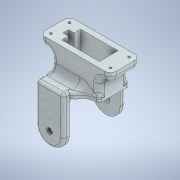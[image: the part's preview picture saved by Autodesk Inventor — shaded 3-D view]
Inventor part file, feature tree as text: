
AUTODESK INVENTOR PART (.ipt)
format: ipt  version: 2021 (Build 250183000, 183)  size: 626,176 bytes
history: native  units: mm
features: sketch x9, extrude x8, fillet x7, projected_geometry x2, plane x1
ambient origin geometry x8: Origin, YZ Plane, XZ Plane, XY Plane, X Axis, Y Axis, Z Axis, Center Point
bodies: Solid1 (feature_tree)
feature tree (27):
  extrude  "Extrusion1"  Depth=30.0mm
  extrude  "Extrusion2"  Depth=2.5mm TaperAngle=0.0deg
  plane  "Work Plane1"
  extrude  "Extrusion3"  Depth=3.5mm TaperAngle=0.0deg
  sketch  "Sketch4"  dims[d8=54.7mm d9=7.8mm d10=6.0mm d11=0.0mm]
  extrude  "Extrusion4"  Depth=7.8mm
  fillet  "Fillet1"  Radius=6.0mm
  extrude  "Extrusion5"  Depth=6.0mm
  extrude  "Extrusion6"  Depth=20.0mm
  extrude  "Extrusion7"  Depth=10.0mm
  fillet  "Fillet2"  Radius=6.0mm
  fillet  "Fillet3"  Radius=27.0mm
  fillet  "Fillet4"  Radius=27.0mm
  fillet  "Fillet5"  Radius=6.0mm
  fillet  "Fillet7"  Radius=7.0mm
  extrude  "Extrusion8"  Depth=10.0mm
  fillet  "Fillet8"  Radius=12.0mm
  sketch  "Sketch1"  dims[d0=20.6mm d1=30.0mm]
  sketch  "Sketch2"  dims[d2=35.0mm d3=2.5mm d4=0.0mm]
  projected_geometry  "Projected Loop1"
  sketch  "Sketch3"  dims[d5=6.0mm d6=3.5mm d7=0.0mm]
  projected_geometry  "Projected Loop2"
  sketch  "Sketch5"  dims[d12=6.0mm d13=0.0mm d14=6.0mm]
  sketch  "Sketch6"  dims[d15=40.0mm d16=20.0mm]
  sketch  "Sketch7"  dims[d17=10.0mm d18=10.0mm d19=6.0mm d20=27.0mm d21=0.0mm d22=27.0mm d23=0.0mm d24=6.0mm d25=7.0mm]
  sketch  "Sketch8"  dims[d26=12.0mm d27=10.0mm d28=12.0mm]
  sketch  "Sketch9"  dims[d29=10.0mm d30=27.0mm d31=0.0mm d32=6.0mm d33=6.0mm d34=3.0mm d35=3.0mm d37=6.0mm d38=2.4mm d39=2.4mm d40=2.4mm d41=2.4mm d42=12.0mm d43=0.0mm d44=8.0mm]
